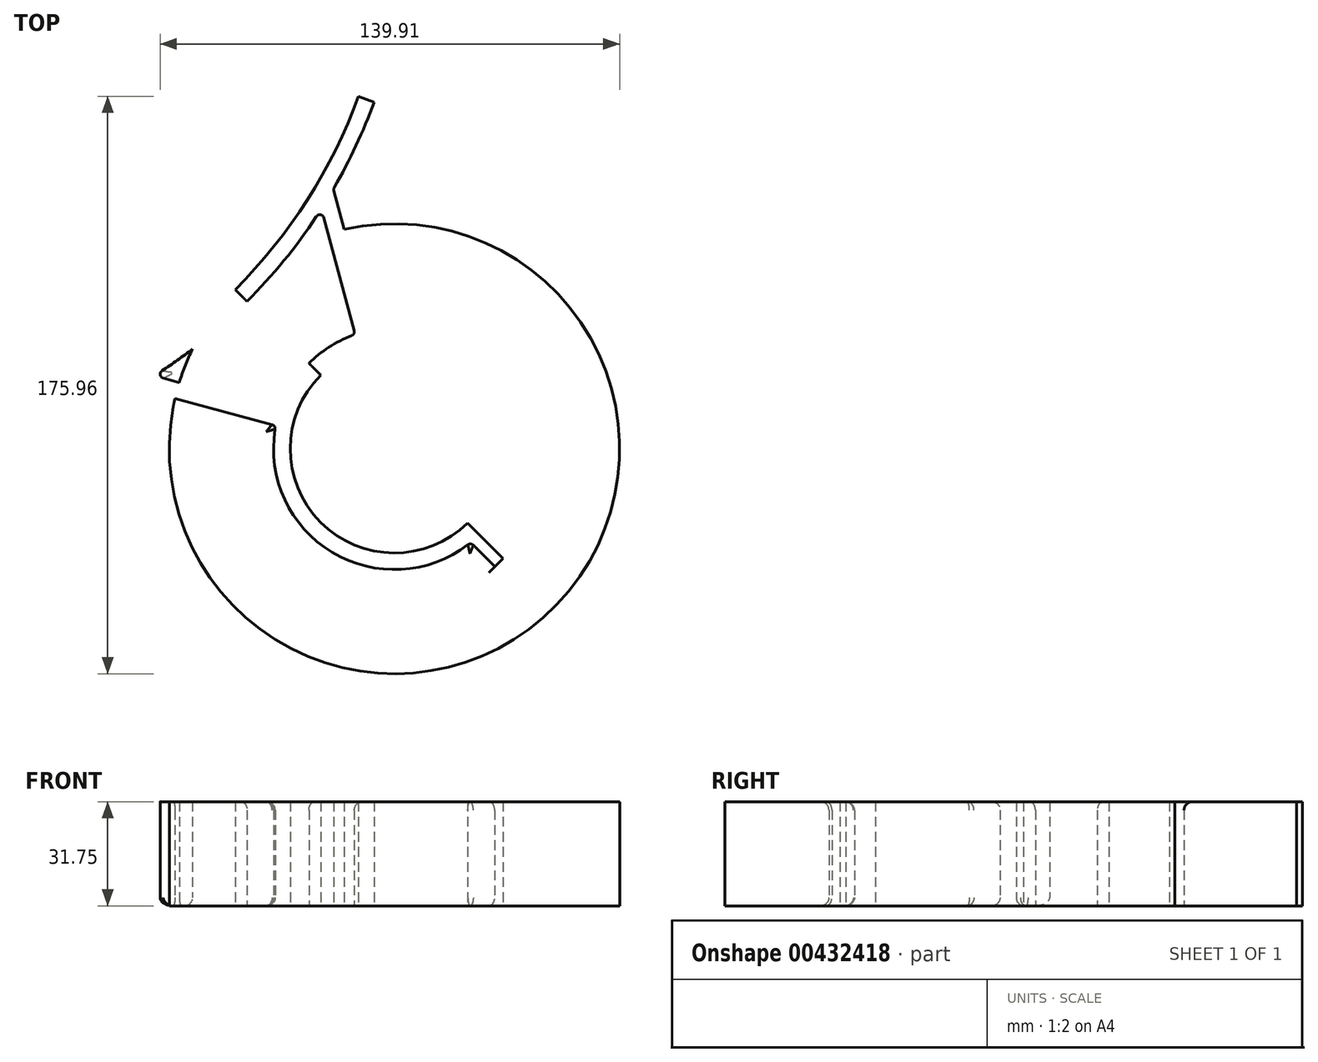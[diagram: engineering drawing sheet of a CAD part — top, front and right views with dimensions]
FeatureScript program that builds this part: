
annotation { "Feature Type Name" : "Feature", "Feature Type Description" : "" }
export const myFeature = defineFeature(function(context is Context, id is Id, definition is map)
    precondition{}
    {
        {
            var Q0;
            Q0=qCreatedBy(makeId("Top.planeOp"),FACE);
            var sketch = newSketch(context, id + "F0", { "sketchPlane" : qUnion([Q0])});
            skCircle(sketch, "E0", {"center": v(0, 0) * mm, "radius": 161.3 * mm});
            skLineSegment(sketch, "E1", {"start": v(0, 0) * mm, "end": v(161.3, 0) * mm});
            skLineSegment(sketch, "E2", {"start": v(0, 0) * mm, "end": v(114.05, -114.05) * mm});
            skLineSegment(sketch, "E3", {"start": v(114.05, -114.05) * mm, "end": v(162.54, -162.54) * mm});
            skArc(sketch, "E4", {"start": v(101.06, -132.16) * mm, "mid": v(205.04, -216.37) * mm, "end": v(147.26, -95.69) * mm});
            skArc(sketch, "E5", {"start": v(185.17, -184.81) * mm, "mid": v(140.1, -140.1) * mm, "end": v(184.81, -185.17) * mm});
            skArc(sketch, "E6.0", {"start": v(191.83, -184.88) * mm, "mid": v(194.12, -143.6) * mm, "end": v(156.62, -126.2) * mm});
            skLineSegment(sketch, "E7", {"start": v(195.95, -195.59) * mm, "end": v(198.46, -193.08) * mm});
            skLineSegment(sketch, "E8", {"start": v(198.46, -193.08) * mm, "end": v(191.94, -186.55) * mm});
            skPoint(sketch, "E9.visualSharp", {"position": v(191.14, -185.75) * mm});
            skArc(sketch, "E9.filletArc", {"start": v(191.83, -184.88) * mm, "mid": v(191.57, -185.74) * mm, "end": v(191.94, -186.55) * mm});
            skArc(sketch, "E10.MirrorCS", {"start": v(184.88, -191.83) * mm, "mid": v(185.74, -191.57) * mm, "end": v(186.55, -191.94) * mm});
            skPoint(sketch, "E11.MirrorP", {"position": v(185.75, -191.14) * mm});
            skLineSegment(sketch, "E12.MirrorCS", {"start": v(193.08, -198.46) * mm, "end": v(186.55, -191.94) * mm});
            skLineSegment(sketch, "E13.MirrorCS", {"start": v(195.59, -195.95) * mm, "end": v(193.08, -198.46) * mm});
            skLineSegment(sketch, "E14.0", {"start": v(188.76, -188.4) * mm, "end": v(195.95, -195.59) * mm});
            skLineSegment(sketch, "E14.1", {"start": v(185.17, -184.81) * mm, "end": v(188.76, -188.4) * mm});
            skLineSegment(sketch, "E15.0", {"start": v(188.4, -188.76) * mm, "end": v(195.59, -195.95) * mm});
            skLineSegment(sketch, "E15.1", {"start": v(184.81, -185.17) * mm, "end": v(188.4, -188.76) * mm});
            skLineSegment(sketch, "E16", {"start": v(153.01, -126.97) * mm, "end": v(142.15, -86.44) * mm});
            skLineSegment(sketch, "E17.0", {"start": v(155.18, -125.27) * mm, "end": v(144.55, -85.58) * mm});
            skLineSegment(sketch, "E18", {"start": v(144.55, -85.58) * mm, "end": v(144.1, -83.9) * mm});
            skLineSegment(sketch, "E19.trimOffspring", {"start": v(150.28, -126.58) * mm, "end": v(141.05, -92.15) * mm});
            skArc(sketch, "E20.trimOffspring", {"start": v(149.5, -128.1) * mm, "mid": v(136.5, -136.5) * mm, "end": v(128.1, -149.5) * mm});
            skPoint(sketch, "E21.visualSharp", {"position": v(150.58, -127.7) * mm});
            skArc(sketch, "E21.filletArc", {"start": v(149.5, -128.1) * mm, "mid": v(150.18, -127.5) * mm, "end": v(150.28, -126.58) * mm});
            skPoint(sketch, "E22.visualSharp", {"position": v(155.49, -126.4) * mm});
            skArc(sketch, "E22.filletArc", {"start": v(155.18, -125.27) * mm, "mid": v(155.72, -126) * mm, "end": v(156.62, -126.2) * mm});
            skArc(sketch, "E23.0", {"start": v(144.22, -82.93) * mm, "mid": v(-117.64, 117.64) * mm, "end": v(82.93, -144.22) * mm});
            skPoint(sketch, "E24.visualSharp", {"position": v(143.96, -83.39) * mm});
            skArc(sketch, "E24.filletArc", {"start": v(144.22, -82.93) * mm, "mid": v(144.07, -83.4) * mm, "end": v(144.1, -83.9) * mm});
            skPoint(sketch, "E25.visualSharp", {"position": v(140.31, -89.4) * mm});
            skArc(sketch, "E25.filletArc", {"start": v(141.05, -92.15) * mm, "mid": v(140.03, -91.22) * mm, "end": v(138.77, -91.78) * mm});
            skArc(sketch, "E26.trimOffspring", {"start": v(142.35, -97) * mm, "mid": v(137.17, -98.83) * mm, "end": v(132.16, -101.06) * mm});
            skArc(sketch, "E27.MirrorCS", {"start": v(92.15, -141.05) * mm, "mid": v(91.22, -140.03) * mm, "end": v(91.78, -138.77) * mm});
            skPoint(sketch, "E28.MirrorP", {"position": v(83.39, -143.96) * mm});
            skArc(sketch, "E29.MirrorCS", {"start": v(97, -142.35) * mm, "mid": v(98.83, -137.17) * mm, "end": v(101.06, -132.16) * mm});
            skArc(sketch, "E30.MirrorCS", {"start": v(128.1, -149.5) * mm, "mid": v(127.5, -150.18) * mm, "end": v(126.58, -150.28) * mm});
            skPoint(sketch, "E31.MirrorP", {"position": v(89.4, -140.31) * mm});
            skPoint(sketch, "E32.MirrorP", {"position": v(127.7, -150.58) * mm});
            skLineSegment(sketch, "E33.MirrorCS", {"start": v(126.97, -153.01) * mm, "end": v(86.44, -142.15) * mm});
            skArc(sketch, "E34.MirrorCS", {"start": v(125.27, -155.18) * mm, "mid": v(126, -155.72) * mm, "end": v(126.2, -156.62) * mm});
            skLineSegment(sketch, "E35.MirrorCS", {"start": v(125.27, -155.18) * mm, "end": v(85.58, -144.55) * mm});
            skPoint(sketch, "E36.MirrorP", {"position": v(126.4, -155.49) * mm});
            skLineSegment(sketch, "E37.MirrorCS", {"start": v(85.58, -144.55) * mm, "end": v(83.9, -144.1) * mm});
            skArc(sketch, "E38.MirrorCS", {"start": v(82.93, -144.22) * mm, "mid": v(83.4, -144.07) * mm, "end": v(83.9, -144.1) * mm});
            skLineSegment(sketch, "E39.MirrorCS", {"start": v(126.58, -150.28) * mm, "end": v(92.15, -141.05) * mm});
            skArc(sketch, "E40.trimOffspring", {"start": v(91.78, -138.77) * mm, "mid": v(117.64, -117.64) * mm, "end": v(138.77, -91.78) * mm});
            skArc(sketch, "E41.trimOffspring", {"start": v(126.2, -156.62) * mm, "mid": v(143.6, -194.12) * mm, "end": v(184.88, -191.83) * mm});
            skLineSegment(sketch, "E42", {"start": v(0, 0) * mm, "end": v(156.34, -56.9) * mm});
            skLineSegment(sketch, "E43.MirrorCS", {"start": v(0, 0) * mm, "end": v(56.9, -156.34) * mm});
            skSolve(sketch);
        }
        {
            var Q0;
            {var subQ4=sQuery(id+"F0.wireOp",EDGE,"E27.MirrorCS");Q0=makeQuery(id+"F0.imprint","IMPRINT",FACE,{"disambiguationData":[TD([[makeQuery(id+"F0.imprint","IMPRINT",EDGE,{"derivedFrom":subQ4}),1.0]])]});}
            var Q1;
            Q1=makeQuery(id+"F0.imprint","IMPRINT",FACE,{"disambiguationData":[TD([[makeQuery(id+"F0.imprint","IMPRINT",EDGE,{"derivedFrom":sQuery(id+"F0.wireOp",EDGE,"E10.MirrorCS")}),1.0]])]});
            var Q2;
            Q2=makeQuery(id+"F0.imprint","IMPRINT",FACE,{"disambiguationData":[TD([[makeQuery(id+"F0.imprint","IMPRINT",EDGE,{"derivedFrom":sQuery(id+"F0.wireOp",EDGE,"E6.0")}),1.0]])]});
            extrude(context, id + "F1", {"entities" : qUnion([Q0, Q1, Q2]), "depth" : 31.75 * mm, "offsetDistance" : 25.4 * mm});
        }
        {
            var Q0;
            Q0=makeQuery(id+"F1.opExtrude","SWEPT_FACE",FACE,{"disambiguationData":[OSD([sQuery(id+"F0.wireOp",EDGE,"E12.MirrorCS")])]});
            var sketch = newSketch(context, id + "F2", { "sketchPlane" : qUnion([Q0])});
            skLineSegment(sketch, "E44", {"start": v(276.86, 31.75) * mm, "end": v(272.24, 31.75) * mm});
            skLineSegment(sketch, "E45", {"start": v(272.24, 31.75) * mm, "end": v(272.24, 25.4) * mm});
            skLineSegment(sketch, "E46", {"start": v(272.24, 25.4) * mm, "end": v(272.24, 6.35) * mm});
            skSolve(sketch);
        }
        {
            var Q0;
            Q0=sQuery(id+"F2.wireOp",VERTEX,"E46.start");
            var Q1;
            Q1=sQuery(id+"F2.wireOp",VERTEX,"E46.end");
            var Q2;
            Q2=makeQuery(id+"F1.opExtrude","SWEPT_BODY",BODY,{"disambiguationData":[OSD([sQuery(id+"F0.wireOp",EDGE,"E0"),sQuery(id+"F0.wireOp",EDGE,"E5"),sQuery(id+"F0.wireOp",EDGE,"E6.0"),sQuery(id+"F0.wireOp",EDGE,"E7"),sQuery(id+"F0.wireOp",EDGE,"E8"),sQuery(id+"F0.wireOp",EDGE,"E9.filletArc"),sQuery(id+"F0.wireOp",EDGE,"E10.MirrorCS"),sQuery(id+"F0.wireOp",EDGE,"E12.MirrorCS"),sQuery(id+"F0.wireOp",EDGE,"E13.MirrorCS"),sQuery(id+"F0.wireOp",EDGE,"E14.0"),sQuery(id+"F0.wireOp",EDGE,"E14.1"),sQuery(id+"F0.wireOp",EDGE,"E15.0"),sQuery(id+"F0.wireOp",EDGE,"E15.1"),sQuery(id+"F0.wireOp",EDGE,"E17.0"),sQuery(id+"F0.wireOp",EDGE,"E18"),sQuery(id+"F0.wireOp",EDGE,"E19.trimOffspring"),sQuery(id+"F0.wireOp",EDGE,"E20.trimOffspring"),sQuery(id+"F0.wireOp",EDGE,"E21.filletArc"),sQuery(id+"F0.wireOp",EDGE,"E22.filletArc"),sQuery(id+"F0.wireOp",EDGE,"E23.0"),sQuery(id+"F0.wireOp",EDGE,"E24.filletArc"),sQuery(id+"F0.wireOp",EDGE,"E25.filletArc"),sQuery(id+"F0.wireOp",EDGE,"E27.MirrorCS"),sQuery(id+"F0.wireOp",EDGE,"E30.MirrorCS"),sQuery(id+"F0.wireOp",EDGE,"E34.MirrorCS"),sQuery(id+"F0.wireOp",EDGE,"E35.MirrorCS"),sQuery(id+"F0.wireOp",EDGE,"E37.MirrorCS"),sQuery(id+"F0.wireOp",EDGE,"E38.MirrorCS"),sQuery(id+"F0.wireOp",EDGE,"E39.MirrorCS"),sQuery(id+"F0.wireOp",EDGE,"E40.trimOffspring"),sQuery(id+"F0.wireOp",EDGE,"E41.trimOffspring"),sQuery(id+"F0.wireOp",EDGE,"E42"),sQuery(id+"F0.wireOp",EDGE,"E43.MirrorCS")])]});
            hole(context, id + "F3", {"style" : HoleStyle.SIMPLE, "endStyle" : HoleEndStyle.THROUGH, "standardTappedOrClearance" : lookupTablePath({ "standard" : "ANSI", "fit" : "Normal (ASME)", "size" : "#6", "type" : "Clearance" }), "standardBlindInLast" : lookupTablePath({ "fit" : "Free", "standard" : "ANSI", "size" : "#6", "type" : "Clearance" }), "holeDiameter" : 3.8 * mm, "isTappedThrough" : true, "tappedDepth" : 12.7 * mm, "tapClearance" : 3, "locations" : qUnion([Q0, Q1]), "scope" : qUnion([Q2])});
        }
        {
            var Q0;
            Q0=makeQuery(id+"F1.opExtrude","CAP_EDGE",EDGE,{"disambiguationData":[OSD([sQuery(id+"F0.wireOp",EDGE,"E41.trimOffspring")])],"isStart":false});
            var Q1;
            Q1=makeQuery(id+"F1.opExtrude","CAP_EDGE",EDGE,{"disambiguationData":[OSD([sQuery(id+"F0.wireOp",EDGE,"E6.0")])],"isStart":false});
            var Q2;
            Q2=makeQuery(id+"F1.opExtrude","CAP_EDGE",EDGE,{"disambiguationData":[OSD([sQuery(id+"F0.wireOp",EDGE,"E41.trimOffspring")])],"isStart":true});
            var Q3;
            Q3=makeQuery(id+"F1.opExtrude","CAP_EDGE",EDGE,{"disambiguationData":[OSD([sQuery(id+"F0.wireOp",EDGE,"E6.0")])],"isStart":true});
            fillet(context, id + "F4", {"entities" : qUnion([Q0, Q1, Q2, Q3]), "radius" : 2.54 * mm, "tangentPropagation" : true, "allowEdgeOverflow" : false});
        }
        {
            var Q0;
            Q0=makeQuery(id+"F1.opExtrude","CAP_EDGE",EDGE,{"disambiguationData":[OSD([sQuery(id+"F0.wireOp",EDGE,"E19.trimOffspring")])],"isStart":false});
            var Q1;
            Q1=makeQuery(id+"F1.opExtrude","CAP_EDGE",EDGE,{"disambiguationData":[OSD([sQuery(id+"F0.wireOp",EDGE,"E39.MirrorCS")])],"isStart":true});
            fillet(context, id + "F5", {"entities" : qUnion([Q0, Q1]), "radius" : 2.54 * mm, "tangentPropagation" : true, "allowEdgeOverflow" : false});
        }
    });
